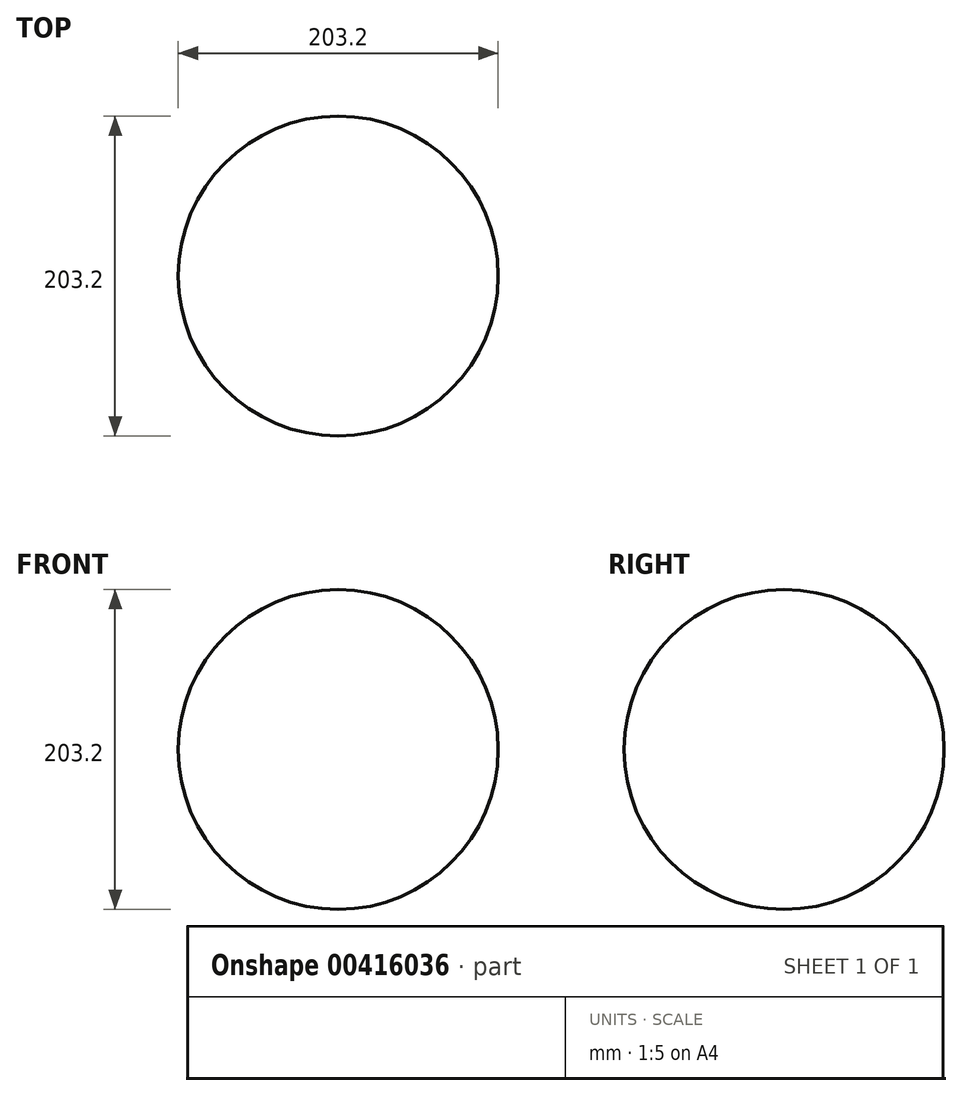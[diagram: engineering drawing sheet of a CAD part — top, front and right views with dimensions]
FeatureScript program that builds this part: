
annotation { "Feature Type Name" : "Feature", "Feature Type Description" : "" }
export const myFeature = defineFeature(function(context is Context, id is Id, definition is map)
    precondition{}
    {
        {
            var Q0;
            Q0=qCreatedBy(makeId("Front.planeOp"),FACE);
            var sketch = newSketch(context, id + "F0", { "sketchPlane" : qUnion([Q0])});
            skArc(sketch, "E0", {"start": v(0, -101.6) * mm, "mid": v(101.6, 0) * mm, "end": v(0, 101.6) * mm});
            skPoint(sketch, "E1", {"position": v(101.6, 0) * mm});
            skLineSegment(sketch, "E2", {"start": v(0, 59.01) * mm, "end": v(0, -59.58) * mm});
            skLineSegment(sketch, "E3", {"start": v(0, 101.6) * mm, "end": v(0, -101.6) * mm});
            skSolve(sketch);
        }
        {
            var Q0;
            {var subQ0=sQuery(id+"F0.wireOp",EDGE,"E0");Q0=makeQuery(id+"F0.imprint","IMPRINT",FACE,{"disambiguationData":[TD([[makeQuery(id+"F0.imprint","IMPRINT",EDGE,{"derivedFrom":subQ0}),1.0]])]});}
            var Q1;
            Q1=sQuery(id+"F0.wireOp",EDGE,"E3");
            revolve(context, id + "F1", {"entities" : qUnion([Q0]), "axis" : qUnion([Q1]), "revolveType" : RevolveType.FULL});
        }
    });
